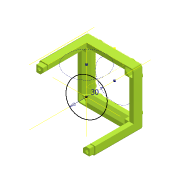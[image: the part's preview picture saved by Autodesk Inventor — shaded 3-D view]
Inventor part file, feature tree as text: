
AUTODESK INVENTOR PART (.ipt)
format: ipt  version: 2022 (Build 260153000, 153)  size: 572,416 bytes
history: native  units: mm
features: projected_geometry x16, sketch x14, extrude x11, plane x7, other x5, hole x3, fillet x2
ambient origin geometry x8: Origin, YZ Plane, XZ Plane, XY Plane, X Axis, Y Axis, Z Axis, Center Point
bodies: Solid1 (feature_tree)
feature tree (58):
  extrude  "Extrusion1"  Depth=49.7mm
  extrude  "Extrusion2"  Depth=8.0mm TaperAngle=0.0deg
  hole  "Hole1"  [1 undecoded]
  sketch  "Sketch4"  dims[d8=3.1mm d9=6.0mm d10=5.5mm d11=4.6mm d12=90.0deg d13=16.0mm d14=20.594885mm d23=2.0mm d30=33.8mm d31=0.0mm]
  sketch  "Sketch5"  dims[d35=33.8mm d36=0.0mm d39=53.8mm]
  other  "Work Axis1"
  other  "Work Axis2"
  fillet  "Fillet1"  Radius=33.8mm
  extrude  "Extrusion3"  Depth=53.8mm
  extrude  "Extrusion4"  Depth=2.0mm
  plane  "Work Plane1"
  extrude  "Extrusion5"  Depth=3.65mm
  hole  "Hole2"  [1 undecoded]
  extrude  "Extrusion6"  Depth=3.65mm
  extrude  "Extrusion7"  Depth=3.78mm
  extrude  "Extrusion8"  Depth=3.78mm
  fillet  "Fillet2"  Radius=3.78mm
  extrude  "Extrusion9"  Depth=10.0mm TaperAngle=0.0deg
  extrude  "Extrusion10"  Depth=4.2mm TaperAngle=0.0deg
  plane  "Work Plane2"
  plane  "Work Plane3"
  hole  "Hole9"  [1 undecoded]
  extrude  "Extrusion11"  Depth=3.4mm
  other  "Work Axis18"
  plane  "Work Plane4"
  sketch  "Sketch23"  dims[d124=3.7mm d125=0.0mm d130=4.2mm d131=0.0mm d132=2.0mm d133=0.5mm d134=3.4mm d135=21.0mm d136=7.38mm d137=3.69mm d138=40.0mm d140=360.0deg d142=4.0mm d143=0.0mm d144=4.95mm d145=2.05mm d146=5.5mm d147=40.0mm d149=360.0deg d151=2.2mm d152=0.0mm d153=3.1mm d154=6.0mm d155=5.5mm d156=3.2mm d157=90.0deg d158=16.0mm d159=20.594885mm d160=5.5mm d161=90.0deg d162=10.0mm d163=0.0mm d164=3.1mm d169=6.1mm d170=6.1mm d171=6.1mm d172=6.1mm d173=1.1mm d174=1.1mm d175=3.78mm d176=3.78mm d177=4.18mm d178=4.18mm d179=4.18mm d180=4.18mm d181=4.18mm d182=4.18mm d183=4.18mm d184=30.0mm d185=0.2mm d186=0.2mm]
  other  "Work Axis19"
  plane  "Arbeitsebene7"
  sketch  "Sketch1"  dims[d0=49.7mm d1=49.7mm]
  sketch  "Sketch2"  dims[d2=7.88mm d3=8.0mm d4=0.0mm]
  projected_geometry  "Projected Loop1"
  sketch  "Sketch3"  dims[d5=34.1mm d6=0.0mm]
  projected_geometry  "Projected Loop3"
  projected_geometry  "Projected Loop4"
  projected_geometry  "Projected Loop5"
  projected_geometry  "Projected Loop6"
  projected_geometry  "Projected Loop7"
  sketch  "Sketch9"  dims[d40=33.8mm d41=0.0mm]
  sketch  "Sketch16"  dims[d42=2.8mm d43=6.0mm d44=3.0mm d45=2.0mm d46=90.0deg d47=12.0mm d48=20.594885mm d96=3.65mm]
  projected_geometry  "Projected Loop14"
  projected_geometry  "Projected Loop15"
  sketch  "Sketch17"  dims[d97=3.65mm d98=3.65mm]
  projected_geometry  "Projected Loop16"
  projected_geometry  "Projected Loop17"
  sketch  "Sketch18"  dims[d99=3.65mm d100=3.65mm]
  sketch  "Sketch19"  dims[d101=3.65mm d102=3.65mm]
  projected_geometry  "Projected Loop22"
  sketch  "Sketch20"  dims[d105=3.78mm d106=3.78mm]
  projected_geometry  "Projected Loop23"
  sketch  "Sketch21"  dims[d107=3.78mm d109=3.78mm d110=3.78mm]
  projected_geometry  "Projected Loop24"
  sketch  "Sketch22"  dims[d112=45.0deg d120=10.0mm d121=0.0mm]
  projected_geometry  "Projected Loop25"
  projected_geometry  "Projected Loop28"
  projected_geometry  "Projected Loop29"
  other  "Work Point1"
  plane  "Work Plane5"
  plane  "Work Plane6"
note: 3 required parameter values undecoded (feature->parameter linkage not recoverable at this tier; creation-order binding heuristic only, values carry confidence <= 0.55)
